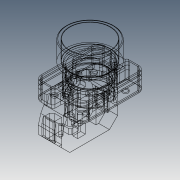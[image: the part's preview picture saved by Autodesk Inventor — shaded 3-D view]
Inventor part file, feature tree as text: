
AUTODESK INVENTOR PART (.ipt)
format: ipt  version: 2018.3 (Build 223284000, 284)  size: 565,248 bytes
history: native  units: in
note: dims shown in document units (in); Inventor stores cm internally (conversion verified against a paired STEP export)
features: other x6, hole x1, sketch x1
ambient origin geometry x8: Origin, YZ Plane, XZ Plane, XY Plane, X Axis, Y Axis, Z Axis, Center Point
bodies: Solid1 (feature_tree), Solid2 (feature_tree), Solid3 (feature_tree), Solid4 (feature_tree), Solid5 (feature_tree), Solid6 (feature_tree)
feature tree (8):
  hole  "Hole1"  [1 undecoded]
  sketch  "Sketch1"  dims[d0=1.1631in d1=0.7874in d2=0.9843in d3=0.13in d4=0.75in d5=0.375in d6=0.25in d7=0.5635in d8=1.0in d9=0.8108in]
  other  "ECX3029-2_1:1"
  other  "ECX3029-2_1:2"
  other  "ECX3029-2_1:3"
  other  "ecx1040_2:1"
  other  "GCX3104 OPERATOR_3:1"
  other  "GCX3104 OPERATOR_3:2"
note: 1 required parameter value undecoded (feature->parameter linkage not recoverable at this tier; creation-order binding heuristic only, values carry confidence <= 0.55)
